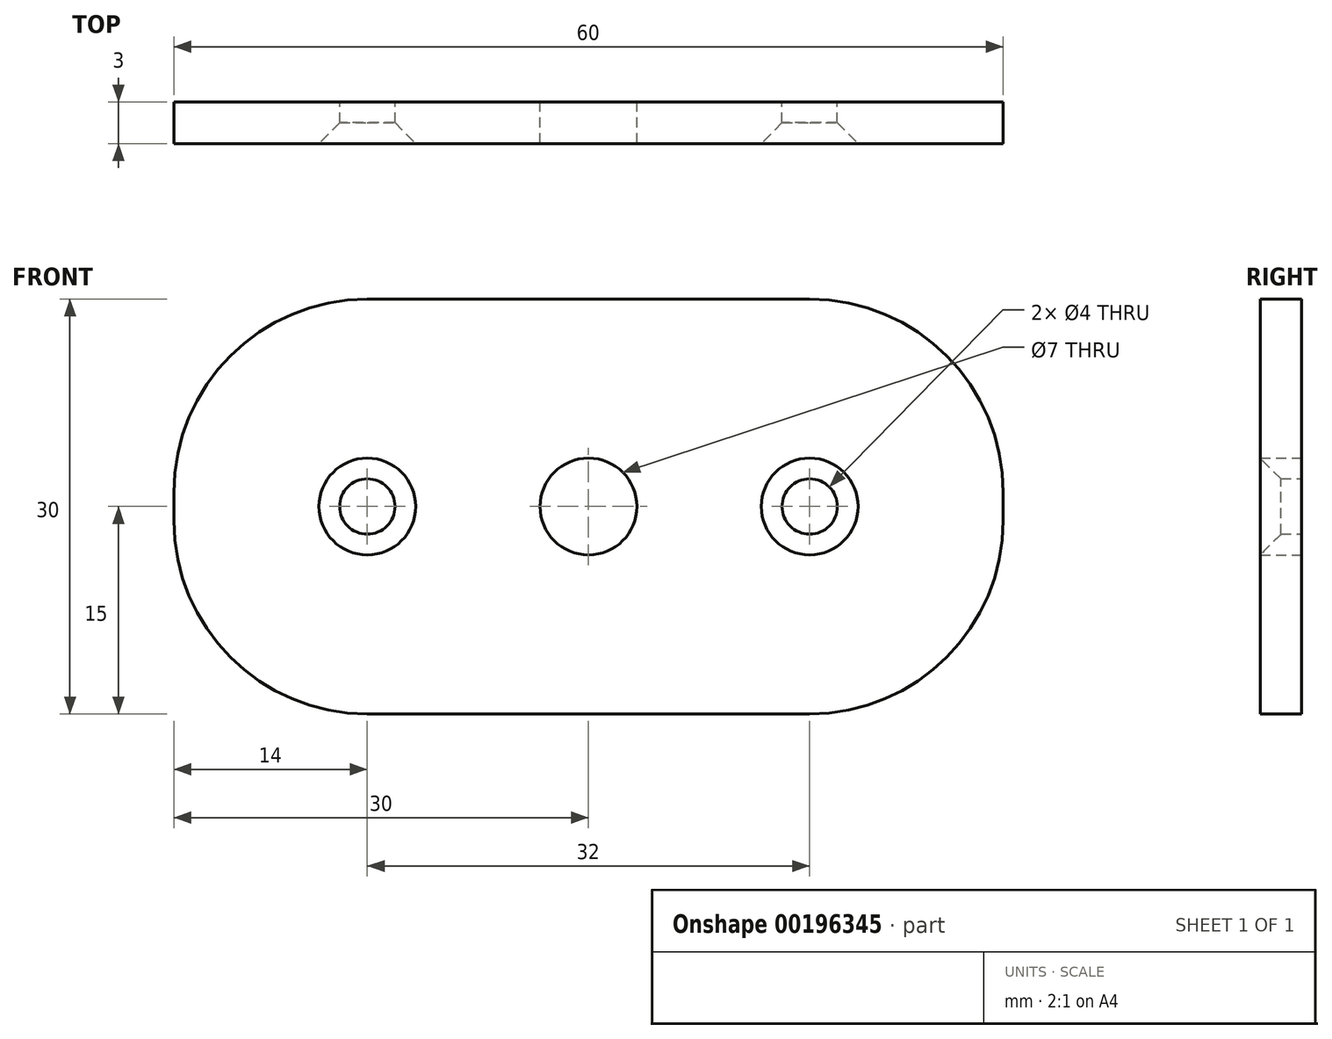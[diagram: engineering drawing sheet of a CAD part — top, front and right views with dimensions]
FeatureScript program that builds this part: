
annotation { "Feature Type Name" : "Feature", "Feature Type Description" : "" }
export const myFeature = defineFeature(function(context is Context, id is Id, definition is map)
    precondition{}
    {
        {
            var Q0;
            Q0=qCreatedBy(makeId("Front.planeOp"),FACE);
            var sketch = newSketch(context, id + "F0", { "sketchPlane" : qUnion([Q0])});
            skLineSegment(sketch, "E0.bottom", {"start": v(16, -15) * mm, "end": v(-16, -15) * mm});
            skLineSegment(sketch, "E0.top", {"start": v(16, 15) * mm, "end": v(-16, 15) * mm});
            skLineSegment(sketch, "E0.left", {"start": v(30, -1) * mm, "end": v(30, 1) * mm});
            skLineSegment(sketch, "E0.right", {"start": v(-30, -1) * mm, "end": v(-30, 1) * mm});
            skPoint(sketch, "E0.middle", {"position": v(0, 0) * mm});
            skPoint(sketch, "E1.visualSharp", {"position": v(30, 15) * mm});
            skArc(sketch, "E1.filletArc", {"start": v(30, 1) * mm, "mid": v(25.9, 10.9) * mm, "end": v(16, 15) * mm});
            skPoint(sketch, "E2.visualSharp", {"position": v(30, -15) * mm});
            skArc(sketch, "E2.filletArc", {"start": v(16, -15) * mm, "mid": v(25.9, -10.9) * mm, "end": v(30, -1) * mm});
            skPoint(sketch, "E3.visualSharp", {"position": v(-30, -15) * mm});
            skArc(sketch, "E3.filletArc", {"start": v(-30, -1) * mm, "mid": v(-25.9, -10.9) * mm, "end": v(-16, -15) * mm});
            skPoint(sketch, "E4.visualSharp", {"position": v(-30, 15) * mm});
            skArc(sketch, "E4.filletArc", {"start": v(-16, 15) * mm, "mid": v(-25.9, 10.9) * mm, "end": v(-30, 1) * mm});
            skLineSegment(sketch, "E5", {"start": v(0, 0) * mm, "end": v(-47.9, 0) * mm, "construction": true});
            skLineSegment(sketch, "E6", {"start": v(0, 0) * mm, "end": v(38.3, 0) * mm, "construction": true});
            skLineSegment(sketch, "E7", {"start": v(-16, 15) * mm, "end": v(-16, -15) * mm, "construction": true});
            skLineSegment(sketch, "E8", {"start": v(16, 15) * mm, "end": v(16, -15) * mm, "construction": true});
            skCircle(sketch, "E9", {"center": v(-16, 0) * mm, "radius": 2 * mm});
            skCircle(sketch, "E10", {"center": v(16, 0) * mm, "radius": 2 * mm});
            skCircle(sketch, "E11", {"center": v(0, 0) * mm, "radius": 3.5 * mm});
            skSolve(sketch);
        }
        {
            var Q0;
            Q0=makeQuery(id+"F0.imprint","IMPRINT",FACE,{"disambiguationData":[TD([[makeQuery(id+"F0.imprint","IMPRINT",EDGE,{"derivedFrom":sQuery(id+"F0.wireOp",EDGE,"E0.bottom")}),-1.0]])]});
            extrude(context, id + "F1", {"entities" : qUnion([Q0]), "depth" : 3 * mm});
        }
        {
            var Q0;
            Q0=makeQuery(id+"F1.opExtrude","CAP_EDGE",EDGE,{"disambiguationData":[OSD([sQuery(id+"F0.wireOp",EDGE,"E9")])],"isStart":false});
            var Q1;
            Q1=makeQuery(id+"F1.opExtrude","CAP_EDGE",EDGE,{"disambiguationData":[OSD([sQuery(id+"F0.wireOp",EDGE,"E10")])],"isStart":false});
            chamfer(context, id + "F2", {"entities" : qUnion([Q0, Q1]), "width" : 1.5 * mm, "tangentPropagation" : true});
        }
    });
